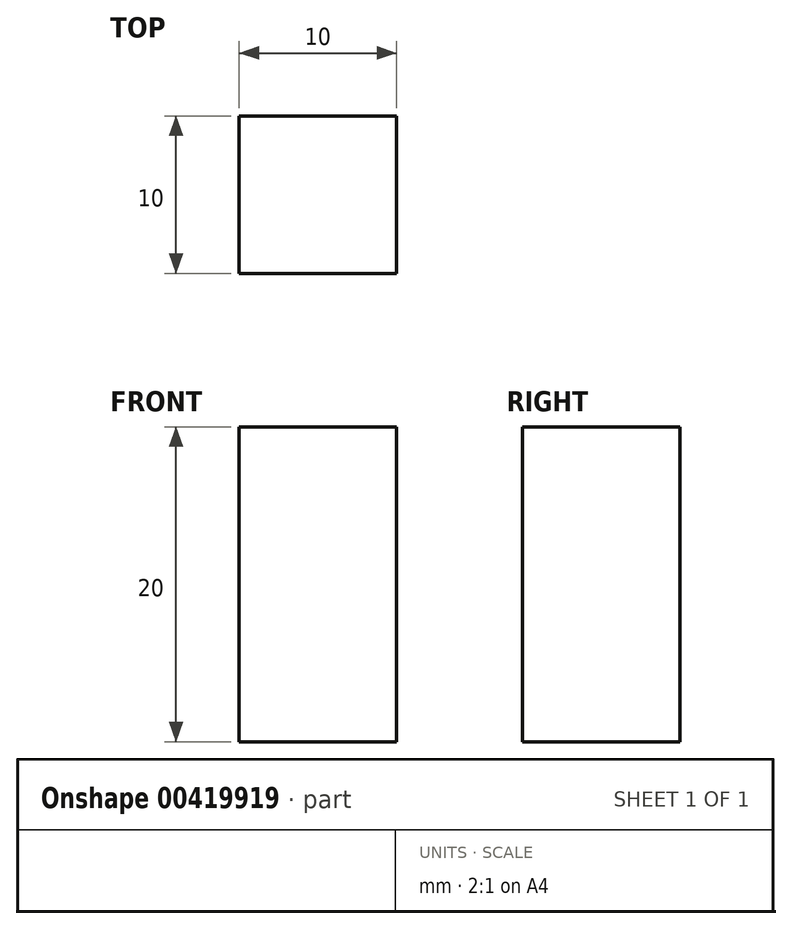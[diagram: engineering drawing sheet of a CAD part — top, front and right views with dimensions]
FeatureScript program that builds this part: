
annotation { "Feature Type Name" : "Feature", "Feature Type Description" : "" }
export const myFeature = defineFeature(function(context is Context, id is Id, definition is map)
    precondition{}
    {
        {
            var Q0;
            Q0=qCreatedBy(makeId("Top.planeOp"),FACE);
            var sketch = newSketch(context, id + "F0", { "sketchPlane" : qUnion([Q0])});
            skLineSegment(sketch, "E0.bottom", {"start": v(0, -1.37) * mm, "end": v(10, -1.37) * mm});
            skLineSegment(sketch, "E0.top", {"start": v(0, 8.63) * mm, "end": v(10, 8.63) * mm});
            skLineSegment(sketch, "E0.left", {"start": v(0, -1.37) * mm, "end": v(0, 8.63) * mm});
            skLineSegment(sketch, "E0.right", {"start": v(10, -1.37) * mm, "end": v(10, 8.63) * mm});
            skSolve(sketch);
        }
        {
            var Q0;
            Q0 = qSketchRegion(id + "F0", true);
            extrude(context, id + "F1", {"entities" : qUnion([Q0]), "depth" : 20 * mm});
        }
    });
